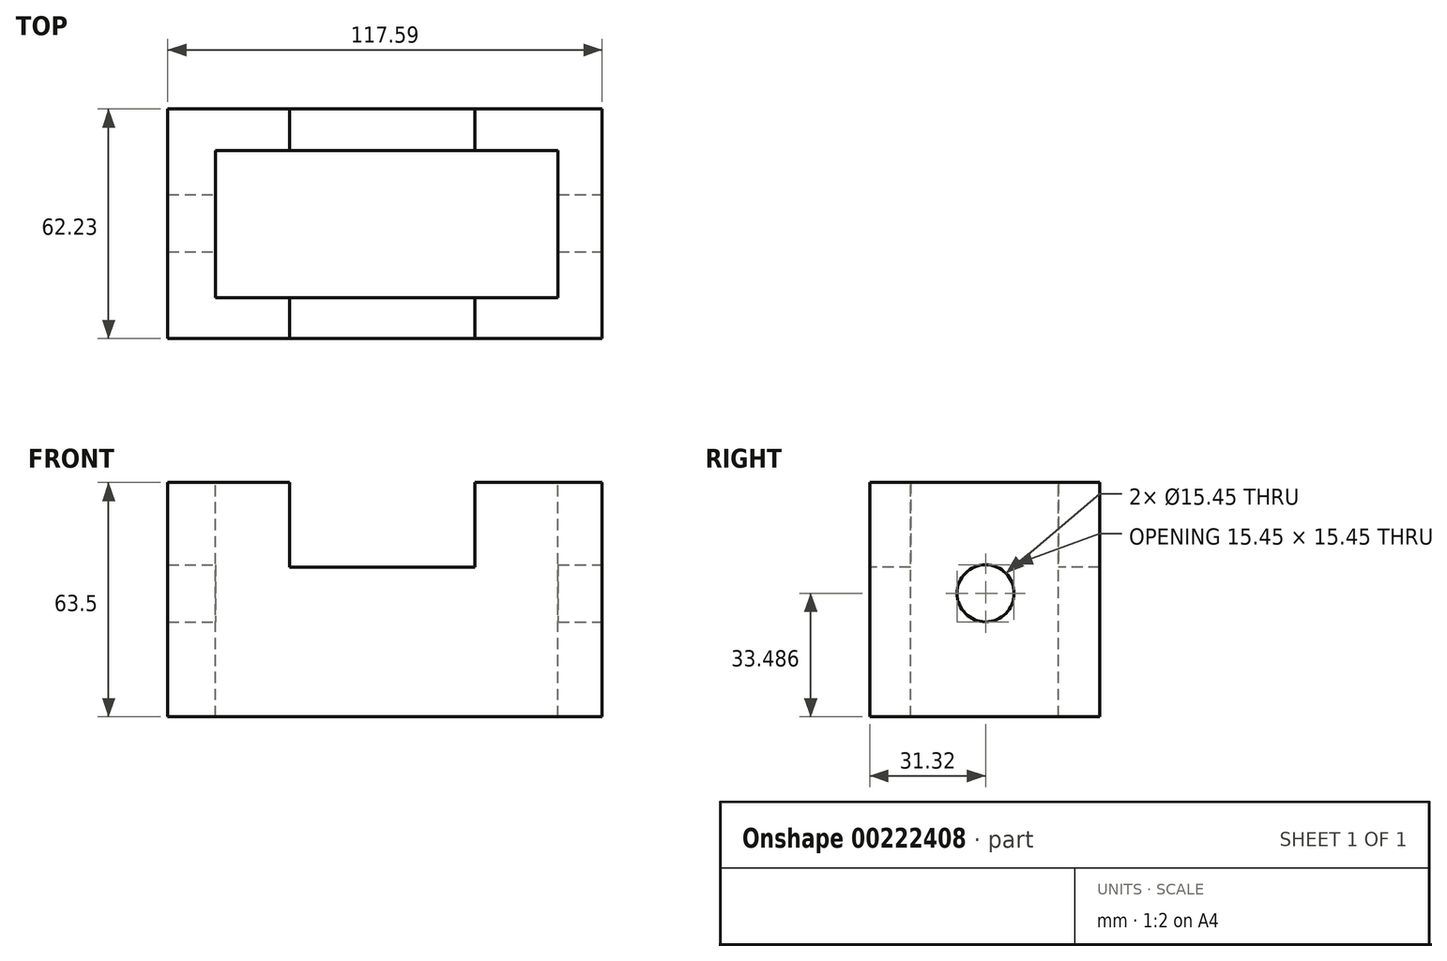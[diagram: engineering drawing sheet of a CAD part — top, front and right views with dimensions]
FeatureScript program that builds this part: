
annotation { "Feature Type Name" : "Feature", "Feature Type Description" : "" }
export const myFeature = defineFeature(function(context is Context, id is Id, definition is map)
    precondition{}
    {
        {
            var Q0;
            Q0=qCreatedBy(makeId("Top.planeOp"),FACE);
            var sketch = newSketch(context, id + "F4", { "sketchPlane" : qUnion([Q0])});
            skLineSegment(sketch, "E0.bottom", {"start": v(-57.02, 30.9) * mm, "end": v(60.57, 30.9) * mm});
            skLineSegment(sketch, "E0.top", {"start": v(-57.02, -31.32) * mm, "end": v(60.57, -31.32) * mm});
            skLineSegment(sketch, "E0.left", {"start": v(-57.02, 30.9) * mm, "end": v(-57.02, -31.32) * mm});
            skLineSegment(sketch, "E0.right", {"start": v(60.57, 30.9) * mm, "end": v(60.57, -31.32) * mm});
            skSolve(sketch);
        }
        {
            var Q0;
            Q0=makeQuery(id+"F4.imprint","IMPRINT",FACE,{"disambiguationData":[TD([[makeQuery(id+"F4.imprint","IMPRINT",EDGE,{"derivedFrom":sQuery(id+"F4.wireOp",EDGE,"E0.bottom")}),-1.0]])]});
            extrude(context, id + "F0", {"entities" : qUnion([Q0]), "depth" : 63.5 * mm});
        }
        {
            var Q0;
            Q0=makeQuery(id+"F0.opExtrude","CAP_FACE",FACE,{"disambiguationData":[OSD([sQuery(id+"F4.wireOp",EDGE,"E0.bottom"),sQuery(id+"F4.wireOp",EDGE,"E0.top"),sQuery(id+"F4.wireOp",EDGE,"E0.left"),sQuery(id+"F4.wireOp",EDGE,"E0.right")])],"isStart":false});
            var sketch = newSketch(context, id + "F5", { "sketchPlane" : qUnion([Q0])});
            skLineSegment(sketch, "E1.bottom", {"start": v(-44.08, 19.68) * mm, "end": v(48.62, 19.68) * mm});
            skLineSegment(sketch, "E1.top", {"start": v(-44.08, -20.26) * mm, "end": v(48.62, -20.26) * mm});
            skLineSegment(sketch, "E1.left", {"start": v(-44.08, 19.68) * mm, "end": v(-44.08, -20.26) * mm});
            skLineSegment(sketch, "E1.right", {"start": v(48.62, 19.68) * mm, "end": v(48.62, -20.26) * mm});
            skSolve(sketch);
        }
        {
            var Q0;
            Q0 = qSketchRegion(id + "F5", true);
            extrude(context, id + "F1", {"entities" : qUnion([Q0]), "operationType" : NewBodyOperationType.REMOVE, "endBound" : BoundingType.THROUGH_ALL, "oppositeDirection" : true, "depth" : 25.4 * mm});
        }
        {
            var Q0;
            Q0=makeQuery(id+"F0.opExtrude","SWEPT_FACE",FACE,{"disambiguationData":[OSD([sQuery(id+"F4.wireOp",EDGE,"E0.right")])]});
            var sketch = newSketch(context, id + "F2", { "sketchPlane" : qUnion([Q0])});
            skCircle(sketch, "E2", {"center": v(0, 33.49) * mm, "radius": 7.73 * mm});
            skSolve(sketch);
        }
        {
            var Q0;
            Q0 = qSketchRegion(id + "F2", true);
            extrude(context, id + "F3", {"entities" : qUnion([Q0]), "operationType" : NewBodyOperationType.REMOVE, "endBound" : BoundingType.THROUGH_ALL, "oppositeDirection" : true, "depth" : 25.4 * mm});
        }
        {
            var Q0;
            Q0=makeQuery(id+"F0.opExtrude","SWEPT_FACE",FACE,{"disambiguationData":[OSD([sQuery(id+"F4.wireOp",EDGE,"E0.top")])]});
            var sketch = newSketch(context, id + "F6", { "sketchPlane" : qUnion([Q0])});
            skLineSegment(sketch, "E3.bottom", {"start": v(-24.05, 63.5) * mm, "end": v(26.15, 63.5) * mm});
            skLineSegment(sketch, "E3.top", {"start": v(-24.05, 40.54) * mm, "end": v(26.15, 40.54) * mm});
            skLineSegment(sketch, "E3.left", {"start": v(-24.05, 63.5) * mm, "end": v(-24.05, 40.54) * mm});
            skLineSegment(sketch, "E3.right", {"start": v(26.15, 63.5) * mm, "end": v(26.15, 40.54) * mm});
            skSolve(sketch);
        }
        {
            var Q0;
            Q0 = qSketchRegion(id + "F6", true);
            extrude(context, id + "F7", {"entities" : qUnion([Q0]), "operationType" : NewBodyOperationType.REMOVE, "endBound" : BoundingType.THROUGH_ALL, "oppositeDirection" : true, "depth" : 25.4 * mm});
        }
    });
